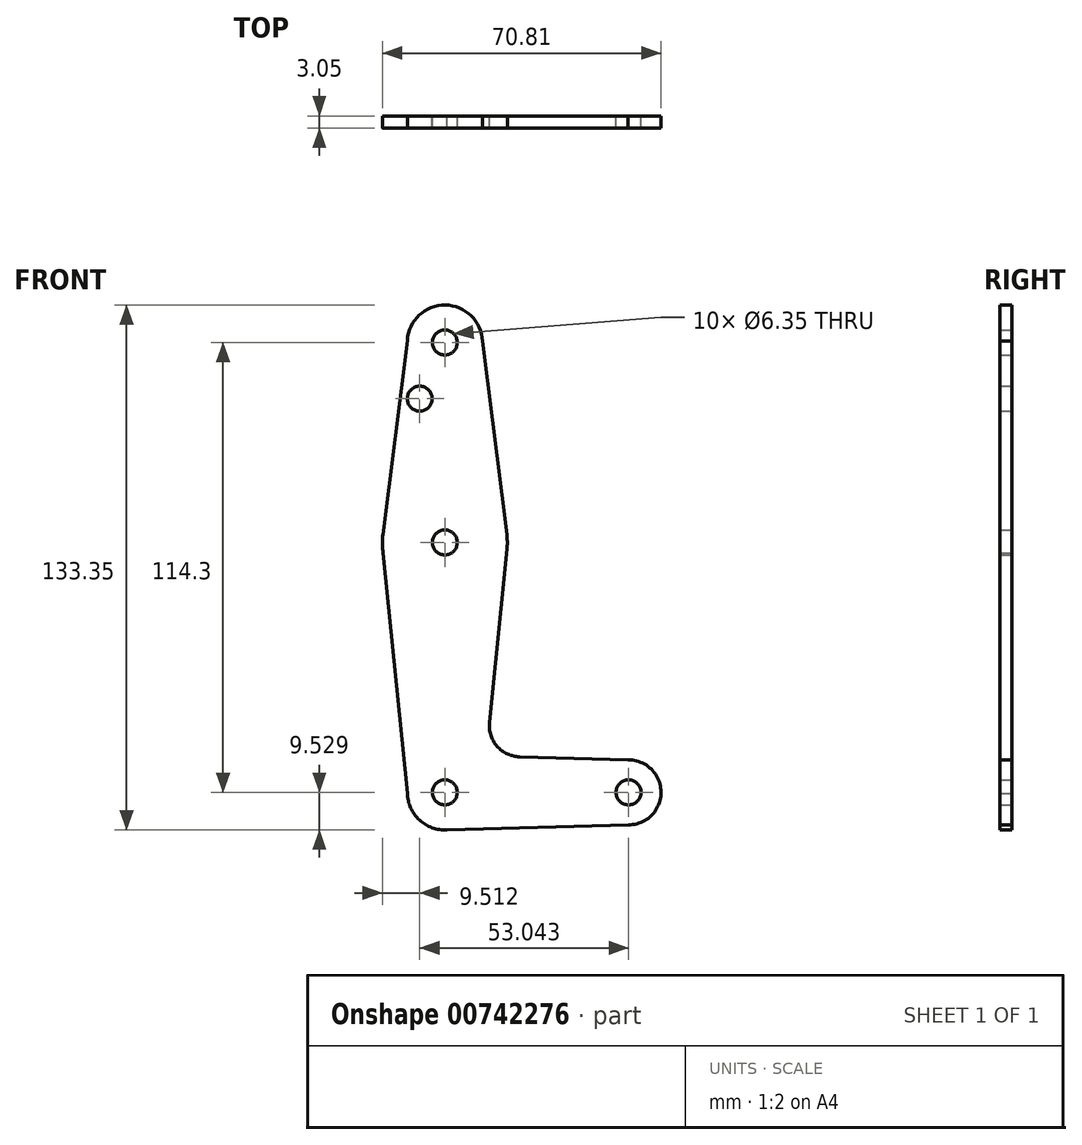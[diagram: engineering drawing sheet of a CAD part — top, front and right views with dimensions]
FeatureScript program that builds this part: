
annotation { "Feature Type Name" : "Feature", "Feature Type Description" : "" }
export const myFeature = defineFeature(function(context is Context, id is Id, definition is map)
    precondition{}
    {
        {
            var Q0;
            Q0=qCreatedBy(makeId("Front.planeOp"),FACE);
            var sketch = newSketch(context, id + "F0", { "sketchPlane" : qUnion([Q0])});
            skCircle(sketch, "E0.MirrorC", {"center": v(-6.43, 36.3) * mm, "radius": 3.18 * mm});
            skCircle(sketch, "E1.MirrorC", {"center": v(-0.06, -0.22) * mm, "radius": 3.18 * mm});
            skCircle(sketch, "E2.MirrorC", {"center": v(-0.06, -63.72) * mm, "radius": 3.18 * mm});
            skCircle(sketch, "E3.MirrorC", {"center": v(-0.06, 50.58) * mm, "radius": 3.18 * mm});
            skLineSegment(sketch, "E4.MirrorCS", {"start": v(15.74, -1.75) * mm, "end": v(11.3, -45.97) * mm});
            skLineSegment(sketch, "E5.MirrorCS", {"start": v(-9.58, -63.98) * mm, "end": v(-15.71, -2.88) * mm});
            skCircle(sketch, "E6.MirrorC", {"center": v(-0.06, 50.58) * mm, "radius": 9.53 * mm});
            skCircle(sketch, "E7.MirrorC", {"center": v(-0.06, -0.22) * mm, "radius": 15.88 * mm});
            skCircle(sketch, "E8.MirrorC", {"center": v(-0.06, -63.72) * mm, "radius": 9.53 * mm});
            skLineSegment(sketch, "E9.MirrorCS", {"start": v(-9.57, 51.13) * mm, "end": v(-15.8, 1.77) * mm});
            skLineSegment(sketch, "E10.MirrorCS", {"start": v(9.24, 52.65) * mm, "end": v(15.69, 1.78) * mm});
            skCircle(sketch, "E11.MirrorC", {"center": v(46.62, -63.72) * mm, "radius": 3.18 * mm});
            skLineSegment(sketch, "E12.MirrorCS", {"start": v(-0.1, -73.25) * mm, "end": v(46.58, -71.98) * mm});
            skCircle(sketch, "E13.MirrorC", {"center": v(46.62, -63.72) * mm, "radius": 8.26 * mm});
            skLineSegment(sketch, "E14.MirrorCS", {"start": v(15.07, -8.47) * mm, "end": v(11.3, -45.97) * mm});
            skArc(sketch, "E15.MirrorCS", {"start": v(19, -54.71) * mm, "mid": v(13.24, -52.02) * mm, "end": v(11.3, -45.97) * mm});
            skLineSegment(sketch, "E16", {"start": v(47.19, -55.49) * mm, "end": v(19, -54.71) * mm});
            skSolve(sketch);
        }
        {
            var Q0;
            Q0 = qSketchRegion(id + "F0", true);
            extrude(context, id + "F1", {"entities" : qUnion([Q0]), "depth" : 3.05 * mm, "offsetDistance" : 25.4 * mm});
        }
    });
